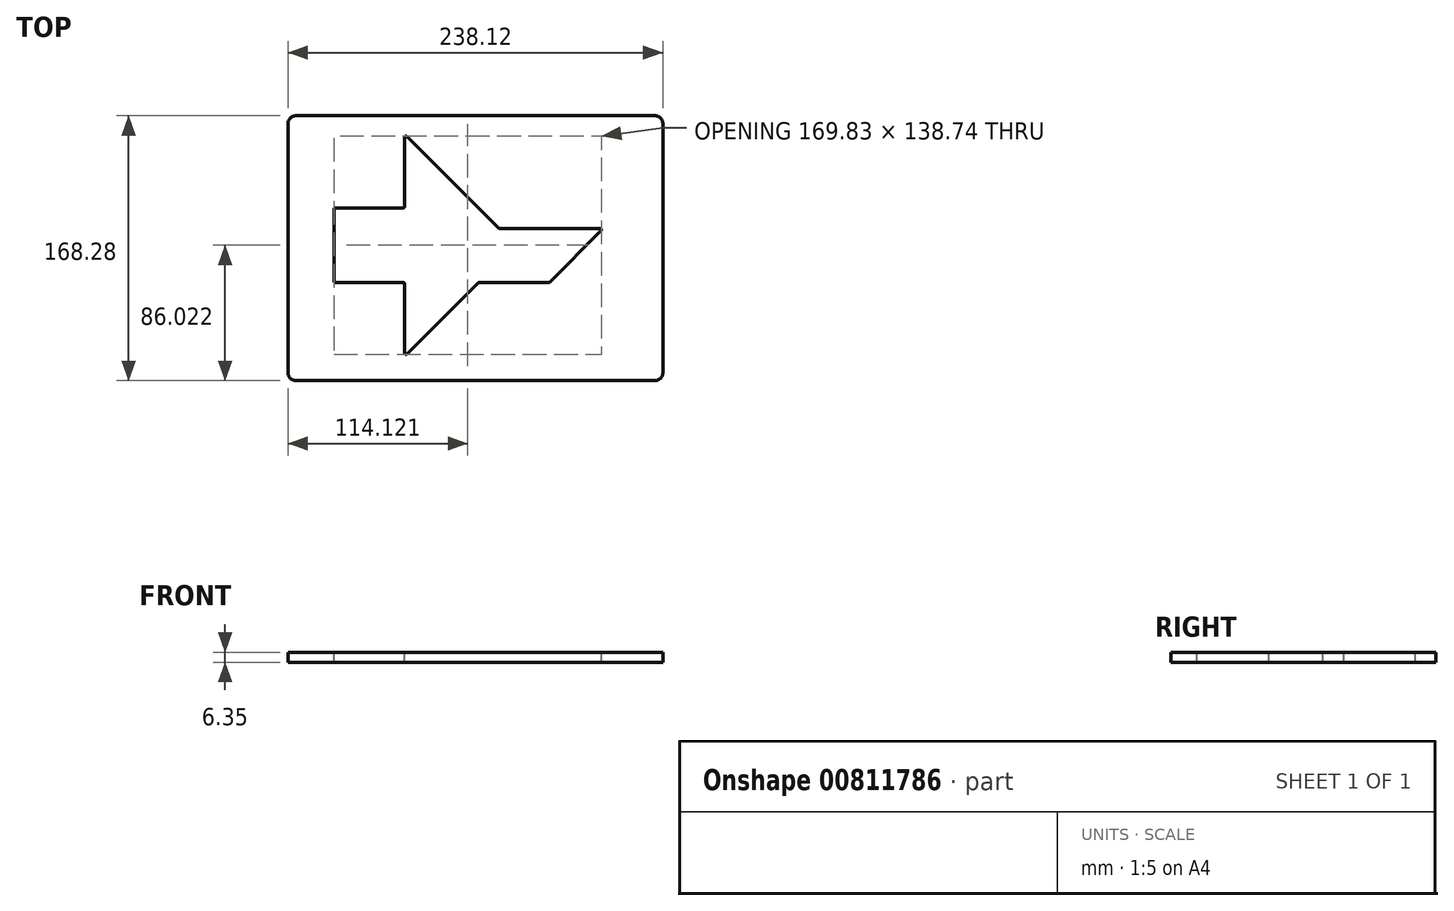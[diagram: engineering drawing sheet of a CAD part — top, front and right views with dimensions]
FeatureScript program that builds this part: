
annotation { "Feature Type Name" : "Feature", "Feature Type Description" : "" }
export const myFeature = defineFeature(function(context is Context, id is Id, definition is map)
    precondition{}
    {
        {
            var Q0;
            Q0=qCreatedBy(makeId("Top.planeOp"),FACE);
            var sketch = newSketch(context, id + "F0", { "sketchPlane" : qUnion([Q0])});
            skLineSegment(sketch, "E0.bottom", {"start": v(-113.98, 84.14) * mm, "end": v(113.98, 84.14) * mm});
            skLineSegment(sketch, "E0.top", {"start": v(-113.98, -84.14) * mm, "end": v(113.98, -84.14) * mm});
            skLineSegment(sketch, "E0.left", {"start": v(-119.06, 79.06) * mm, "end": v(-119.06, -79.06) * mm});
            skLineSegment(sketch, "E0.right", {"start": v(119.06, 79.06) * mm, "end": v(119.06, -79.06) * mm});
            skPoint(sketch, "E0.middle", {"position": v(0, 0) * mm});
            skPoint(sketch, "E1.visualSharp", {"position": v(-119.06, 84.14) * mm});
            skArc(sketch, "E1.filletArc", {"start": v(-113.98, 84.14) * mm, "mid": v(-117.57, 82.65) * mm, "end": v(-119.06, 79.06) * mm});
            skPoint(sketch, "E2.visualSharp", {"position": v(-119.06, -84.14) * mm});
            skArc(sketch, "E2.filletArc", {"start": v(-119.06, -79.06) * mm, "mid": v(-117.57, -82.65) * mm, "end": v(-113.98, -84.14) * mm});
            skPoint(sketch, "E3.visualSharp", {"position": v(119.06, -84.14) * mm});
            skArc(sketch, "E3.filletArc", {"start": v(113.98, -84.14) * mm, "mid": v(117.57, -82.65) * mm, "end": v(119.06, -79.06) * mm});
            skPoint(sketch, "E4.visualSharp", {"position": v(119.06, 84.14) * mm});
            skArc(sketch, "E4.filletArc", {"start": v(119.06, 79.06) * mm, "mid": v(117.57, 82.65) * mm, "end": v(113.98, 84.14) * mm});
            skSolve(sketch);
        }
        {
            var Q0;
            Q0 = qSketchRegion(id + "F0", true);
            extrude(context, id + "F1", {"entities" : qUnion([Q0]), "depth" : 6.35 * mm, "offsetDistance" : 25.4 * mm});
        }
        {
            var Q0;
            Q0=makeQuery(id+"F1.opExtrude","CAP_FACE",FACE,{"disambiguationData":[OSD([sQuery(id+"F0.wireOp",EDGE,"E0.bottom"),sQuery(id+"F0.wireOp",EDGE,"E0.top"),sQuery(id+"F0.wireOp",EDGE,"E0.left"),sQuery(id+"F0.wireOp",EDGE,"E0.right"),sQuery(id+"F0.wireOp",EDGE,"E1.filletArc"),sQuery(id+"F0.wireOp",EDGE,"E2.filletArc"),sQuery(id+"F0.wireOp",EDGE,"E3.filletArc"),sQuery(id+"F0.wireOp",EDGE,"E4.filletArc")])],"isStart":false});
            var sketch = newSketch(context, id + "F2", { "sketchPlane" : qUnion([Q0])});
            skLineSegment(sketch, "E5", {"start": v(-88.58, -20.61) * mm, "end": v(-43.62, -20.61) * mm});
            skLineSegment(sketch, "E6", {"start": v(-43.62, -20.61) * mm, "end": v(-43.62, -65.54) * mm});
            skLineSegment(sketch, "E7", {"start": v(-43.62, -65.54) * mm, "end": v(1.28, -20.64) * mm});
            skLineSegment(sketch, "E8", {"start": v(1.28, -20.64) * mm, "end": v(46.23, -20.64) * mm});
            skLineSegment(sketch, "E9", {"start": v(46.23, -20.64) * mm, "end": v(78.02, 11.15) * mm});
            skLineSegment(sketch, "E10", {"start": v(78.02, 11.15) * mm, "end": v(14.52, 11.15) * mm});
            skLineSegment(sketch, "E11", {"start": v(14.52, 11.15) * mm, "end": v(-43.62, 69.3) * mm});
            skLineSegment(sketch, "E12", {"start": v(-43.62, 69.3) * mm, "end": v(-43.62, 24.34) * mm});
            skLineSegment(sketch, "E13", {"start": v(-43.62, 24.34) * mm, "end": v(-88.58, 24.34) * mm});
            skLineSegment(sketch, "E14", {"start": v(-88.58, 24.34) * mm, "end": v(-88.58, -20.61) * mm});
            skSolve(sketch);
        }
        {
            var Q0;
            Q0 = qSketchRegion(id + "F2", true);
            extrude(context, id + "F3", {"entities" : qUnion([Q0]), "operationType" : NewBodyOperationType.REMOVE, "endBound" : BoundingType.THROUGH_ALL, "oppositeDirection" : true, "depth" : 25.4 * mm, "offsetDistance" : 25.4 * mm});
        }
        {
            var Q0;
            Q0=makeQuery(id+"F1.opExtrude","CAP_FACE",FACE,{"disambiguationData":[OSD([sQuery(id+"F0.wireOp",EDGE,"E0.bottom"),sQuery(id+"F0.wireOp",EDGE,"E0.top"),sQuery(id+"F0.wireOp",EDGE,"E0.left"),sQuery(id+"F0.wireOp",EDGE,"E0.right"),sQuery(id+"F0.wireOp",EDGE,"E1.filletArc"),sQuery(id+"F0.wireOp",EDGE,"E2.filletArc"),sQuery(id+"F0.wireOp",EDGE,"E3.filletArc"),sQuery(id+"F0.wireOp",EDGE,"E4.filletArc")])],"isStart":false});
            var sketch = newSketch(context, id + "F4", { "sketchPlane" : qUnion([Q0])});
            skLineSegment(sketch, "E15.0", {"start": v(79.19, 12.42) * mm, "end": v(15.38, 12.42) * mm});
            skLineSegment(sketch, "E15.1", {"start": v(47, -21.68) * mm, "end": v(79.75, 11.08) * mm});
            skLineSegment(sketch, "E15.2", {"start": v(14.82, 12.65) * mm, "end": v(-43.55, 71.02) * mm});
            skLineSegment(sketch, "E15.3", {"start": v(2.13, -21.9) * mm, "end": v(46.43, -21.9) * mm});
            skLineSegment(sketch, "E15.4", {"start": v(-43.55, -67.26) * mm, "end": v(1.57, -22.14) * mm});
            skLineSegment(sketch, "E15.5", {"start": v(-44.9, -22.67) * mm, "end": v(-44.9, -66.7) * mm});
            skLineSegment(sketch, "E15.6", {"start": v(-44.9, 70.47) * mm, "end": v(-44.9, 26.4) * mm});
            skLineSegment(sketch, "E15.7", {"start": v(-45.68, 25.61) * mm, "end": v(-89.07, 25.61) * mm});
            skLineSegment(sketch, "E15.8", {"start": v(-89.85, 24.83) * mm, "end": v(-89.85, -21.1) * mm});
            skLineSegment(sketch, "E15.9", {"start": v(-89.07, -21.88) * mm, "end": v(-45.68, -21.88) * mm});
            skPoint(sketch, "E16.visualSharp", {"position": v(-44.9, 72.37) * mm});
            skArc(sketch, "E16.filletArc", {"start": v(-43.55, 71.02) * mm, "mid": v(-44.4, 71.2) * mm, "end": v(-44.9, 70.47) * mm});
            skPoint(sketch, "E17.visualSharp", {"position": v(15.05, 12.42) * mm});
            skArc(sketch, "E17.filletArc", {"start": v(14.82, 12.65) * mm, "mid": v(15.08, 12.48) * mm, "end": v(15.38, 12.42) * mm});
            skPoint(sketch, "E18.visualSharp", {"position": v(81.1, 12.42) * mm});
            skArc(sketch, "E18.filletArc", {"start": v(79.75, 11.08) * mm, "mid": v(79.92, 11.94) * mm, "end": v(79.19, 12.42) * mm});
            skPoint(sketch, "E19.visualSharp", {"position": v(46.76, -21.9) * mm});
            skArc(sketch, "E19.filletArc", {"start": v(46.43, -21.9) * mm, "mid": v(46.74, -21.85) * mm, "end": v(47, -21.68) * mm});
            skPoint(sketch, "E20.visualSharp", {"position": v(1.8, -21.9) * mm});
            skArc(sketch, "E20.filletArc", {"start": v(2.13, -21.9) * mm, "mid": v(1.83, -21.97) * mm, "end": v(1.57, -22.14) * mm});
            skPoint(sketch, "E21.visualSharp", {"position": v(-44.9, -68.6) * mm});
            skArc(sketch, "E21.filletArc", {"start": v(-44.9, -66.7) * mm, "mid": v(-44.4, -67.43) * mm, "end": v(-43.55, -67.26) * mm});
            skPoint(sketch, "E22.visualSharp", {"position": v(-44.9, -21.88) * mm});
            skArc(sketch, "E22.filletArc", {"start": v(-44.9, -22.67) * mm, "mid": v(-45.13, -22.11) * mm, "end": v(-45.68, -21.88) * mm});
            skPoint(sketch, "E23.visualSharp", {"position": v(-89.85, -21.88) * mm});
            skArc(sketch, "E23.filletArc", {"start": v(-89.85, -21.1) * mm, "mid": v(-89.62, -21.65) * mm, "end": v(-89.07, -21.88) * mm});
            skPoint(sketch, "E24.visualSharp", {"position": v(-89.85, 25.61) * mm});
            skArc(sketch, "E24.filletArc", {"start": v(-89.07, 25.61) * mm, "mid": v(-89.62, 25.38) * mm, "end": v(-89.85, 24.83) * mm});
            skPoint(sketch, "E25.visualSharp", {"position": v(-44.9, 25.61) * mm});
            skArc(sketch, "E25.filletArc", {"start": v(-45.68, 25.61) * mm, "mid": v(-45.13, 25.84) * mm, "end": v(-44.9, 26.4) * mm});
            skSolve(sketch);
        }
        {
            var Q0;
            Q0 = qSketchRegion(id + "F4", true);
            extrude(context, id + "F5", {"entities" : qUnion([Q0]), "operationType" : NewBodyOperationType.REMOVE, "endBound" : BoundingType.THROUGH_ALL, "oppositeDirection" : true, "depth" : 25.4 * mm, "offsetDistance" : 25.4 * mm});
        }
    });
